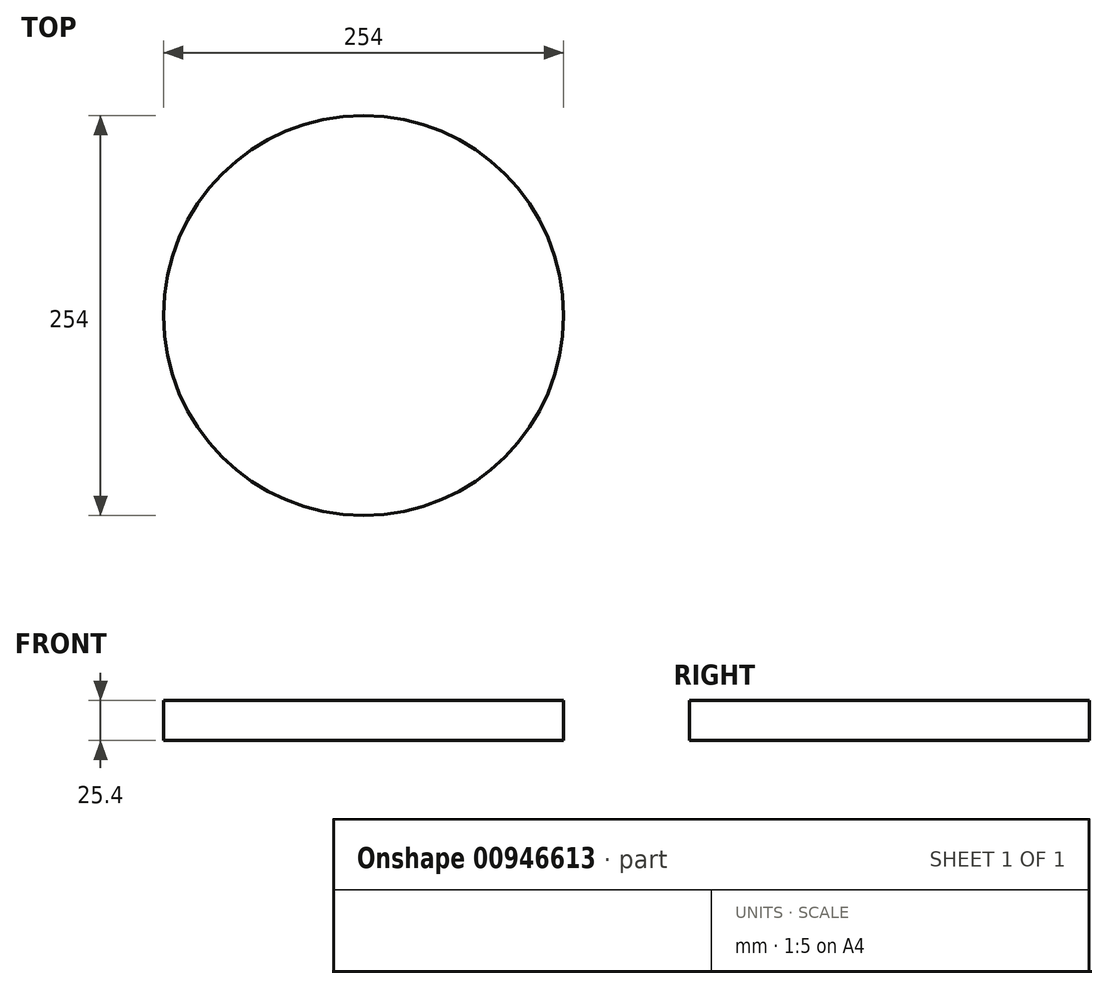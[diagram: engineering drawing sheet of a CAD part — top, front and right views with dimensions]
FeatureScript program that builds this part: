
annotation { "Feature Type Name" : "Feature", "Feature Type Description" : "" }
export const myFeature = defineFeature(function(context is Context, id is Id, definition is map)
    precondition{}
    {
        {
            var Q0;
            Q0=qCreatedBy(makeId("Top.planeOp"),FACE);
            var sketch = newSketch(context, id + "F0", { "sketchPlane" : qUnion([Q0])});
            skCircle(sketch, "E0", {"center": v(-19.85, -5.97) * mm, "radius": 127 * mm});
            skSolve(sketch);
        }
        {
            var Q0;
            Q0=makeQuery(id+"F0.imprint","IMPRINT",FACE,{"disambiguationData":[TD([[makeQuery(id+"F0.imprint","IMPRINT",EDGE,{"derivedFrom":sQuery(id+"F0.wireOp",EDGE,"E0")}),1.0]])]});
            extrude(context, id + "F1", {"entities" : qUnion([Q0]), "depth" : 25.4 * mm, "offsetDistance" : 25.4 * mm});
        }
    });
